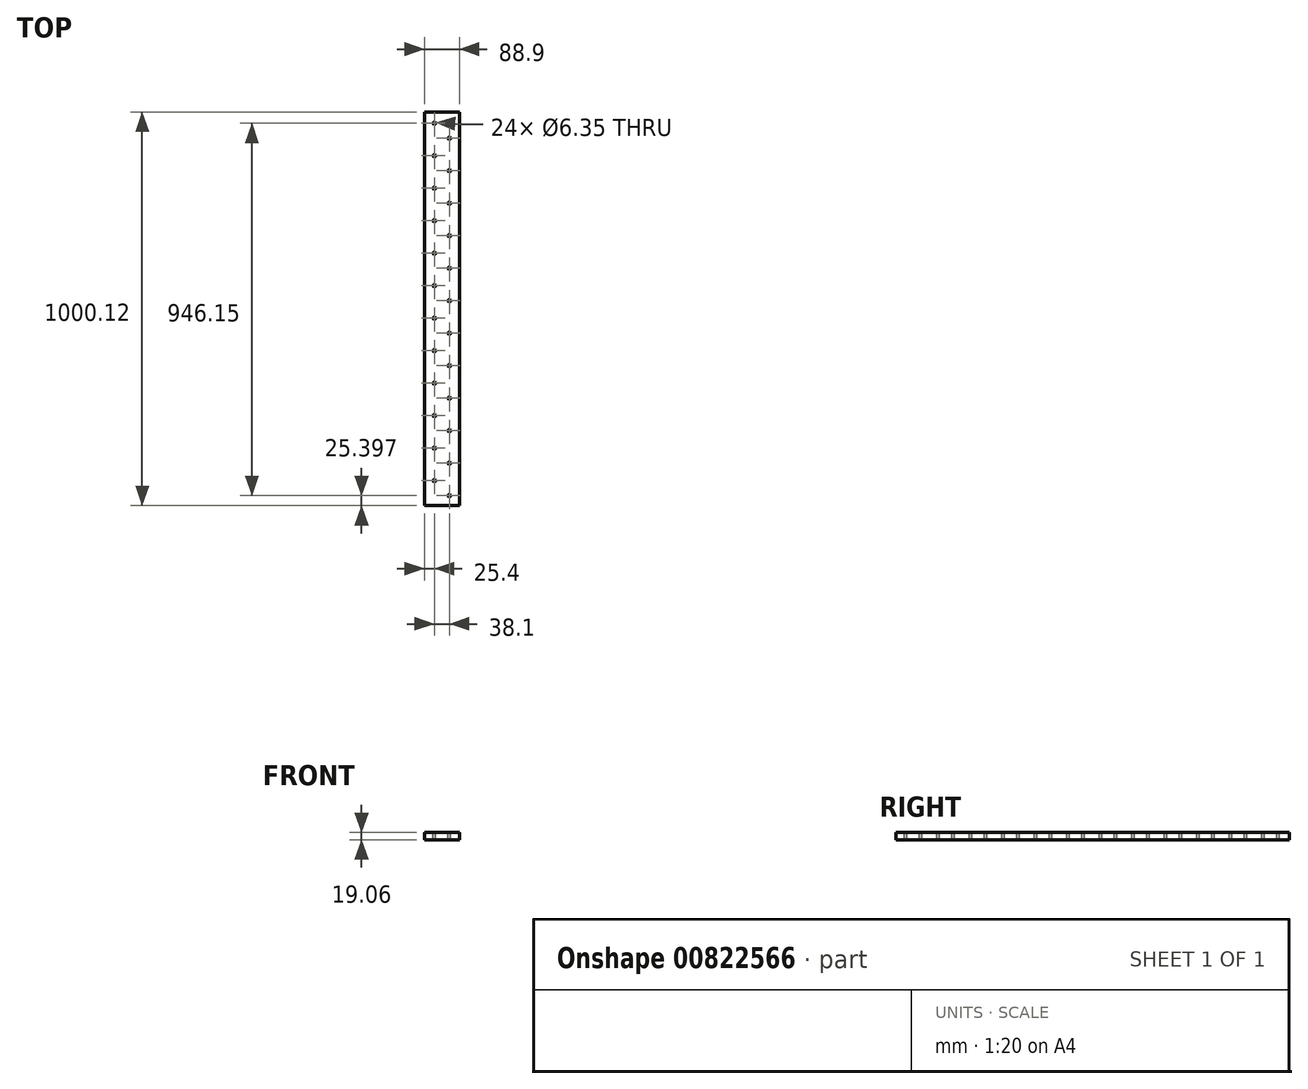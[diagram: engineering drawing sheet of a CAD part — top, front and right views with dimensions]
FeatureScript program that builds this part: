
annotation { "Feature Type Name" : "Feature", "Feature Type Description" : "" }
export const myFeature = defineFeature(function(context is Context, id is Id, definition is map)
    precondition{}
    {
        {
            var Q0;
            Q0=qCreatedBy(makeId("Front.planeOp"),FACE);
            var sketch = newSketch(context, id + "F0", { "sketchPlane" : qUnion([Q0])});
            skLineSegment(sketch, "E0.bottom", {"start": v(-44.45, 9.52) * mm, "end": v(44.45, 9.52) * mm});
            skLineSegment(sketch, "E0.top", {"start": v(-44.45, -9.53) * mm, "end": v(44.45, -9.53) * mm});
            skLineSegment(sketch, "E0.left", {"start": v(-44.45, 9.52) * mm, "end": v(-44.45, -9.53) * mm});
            skLineSegment(sketch, "E0.right", {"start": v(44.45, 9.52) * mm, "end": v(44.45, -9.53) * mm});
            skLineSegment(sketch, "E1", {"start": v(-44.45, -9.53) * mm, "end": v(44.45, 9.52) * mm, "construction": true});
            skSolve(sketch);
        }
        {
            var Q0;
            Q0=makeQuery(id+"F0.imprint","IMPRINT",FACE,{"disambiguationData":[TD([[makeQuery(id+"F0.imprint","IMPRINT",EDGE,{"derivedFrom":sQuery(id+"F0.wireOp",EDGE,"E0.bottom")}),-1.0]])]});
            extrude(context, id + "F1", {"entities" : qUnion([Q0]), "endBound" : BoundingType.SYMMETRIC, "depth" : 1000.12 * mm, "offsetDistance" : 25.4 * mm});
        }
        {
            var Q0;
            Q0=makeQuery(id+"F1.opExtrude","SWEPT_FACE",FACE,{"disambiguationData":[OSD([sQuery(id+"F0.wireOp",EDGE,"E0.bottom")])]});
            var sketch = newSketch(context, id + "F2", { "sketchPlane" : qUnion([Q0])});
            skLineSegment(sketch, "E2.bottom", {"start": v(-19.05, -436.56) * mm, "end": v(19.05, -436.56) * mm, "construction": true});
            skLineSegment(sketch, "E2.left", {"start": v(-19.05, -436.56) * mm, "end": v(-19.05, -474.66) * mm, "construction": true});
            skLineSegment(sketch, "E2.right", {"start": v(19.05, -436.56) * mm, "end": v(19.05, -474.66) * mm, "construction": true});
            skLineSegment(sketch, "E3", {"start": v(-19.05, -474.66) * mm, "end": v(19.05, -474.66) * mm, "construction": true});
            skLineSegment(sketch, "E4", {"start": v(0, -474.66) * mm, "end": v(0, -500.06) * mm, "construction": true});
            skCircle(sketch, "E5", {"center": v(19.05, -474.66) * mm, "radius": 3.18 * mm});
            skCircle(sketch, "E6", {"center": v(-19.05, -436.56) * mm, "radius": 3.18 * mm});
            skCircle(sketch, "E7.0.1.0", {"center": v(-19.05, -354.01) * mm, "radius": 3.18 * mm});
            skCircle(sketch, "E7.0.1.1", {"center": v(19.05, -392.11) * mm, "radius": 3.18 * mm});
            skCircle(sketch, "E7.0.2.0", {"center": v(-19.05, -271.46) * mm, "radius": 3.18 * mm});
            skCircle(sketch, "E7.0.2.1", {"center": v(19.05, -309.56) * mm, "radius": 3.18 * mm});
            skCircle(sketch, "E7.0.3.0", {"center": v(-19.05, -188.91) * mm, "radius": 3.18 * mm});
            skCircle(sketch, "E7.0.3.1", {"center": v(19.05, -227.01) * mm, "radius": 3.18 * mm});
            skCircle(sketch, "E7.0.4.0", {"center": v(-19.05, -106.36) * mm, "radius": 3.18 * mm});
            skCircle(sketch, "E7.0.4.1", {"center": v(19.05, -144.46) * mm, "radius": 3.18 * mm});
            skCircle(sketch, "E7.0.5.0", {"center": v(-19.05, -23.81) * mm, "radius": 3.18 * mm});
            skCircle(sketch, "E7.0.5.1", {"center": v(19.05, -61.91) * mm, "radius": 3.18 * mm});
            skCircle(sketch, "E7.0.6.0", {"center": v(-19.05, 58.74) * mm, "radius": 3.18 * mm});
            skCircle(sketch, "E7.0.6.1", {"center": v(19.05, 20.64) * mm, "radius": 3.18 * mm});
            skCircle(sketch, "E7.0.7.0", {"center": v(-19.05, 141.29) * mm, "radius": 3.18 * mm});
            skCircle(sketch, "E7.0.7.1", {"center": v(19.05, 103.19) * mm, "radius": 3.18 * mm});
            skCircle(sketch, "E7.0.8.0", {"center": v(-19.05, 223.84) * mm, "radius": 3.18 * mm});
            skCircle(sketch, "E7.0.8.1", {"center": v(19.05, 185.74) * mm, "radius": 3.18 * mm});
            skCircle(sketch, "E7.0.9.0", {"center": v(-19.05, 306.39) * mm, "radius": 3.18 * mm});
            skCircle(sketch, "E7.0.9.1", {"center": v(19.05, 268.29) * mm, "radius": 3.18 * mm});
            skCircle(sketch, "E7.0.10.0", {"center": v(-19.05, 388.94) * mm, "radius": 3.18 * mm});
            skCircle(sketch, "E7.0.10.1", {"center": v(19.05, 350.84) * mm, "radius": 3.18 * mm});
            skLineSegment(sketch, "E7.direction1", {"start": v(-19.05, -436.56) * mm, "end": v(8.37, -436.56) * mm, "construction": true});
            skLineSegment(sketch, "E7.direction2", {"start": v(-19.05, -436.56) * mm, "end": v(-19.05, -354.01) * mm, "construction": true});
            skCircle(sketch, "E8.0.0.11", {"center": v(-19.05, 471.49) * mm, "radius": 3.18 * mm});
            skCircle(sketch, "E8.2.0.11", {"center": v(19.05, 433.39) * mm, "radius": 3.18 * mm});
            skSolve(sketch);
        }
        {
            var Q0;
            Q0=qSketchRegion(id+"F2",true);
            extrude(context, id + "F3", {"entities" : qUnion([Q0]), "operationType" : NewBodyOperationType.REMOVE, "endBound" : BoundingType.UP_TO_NEXT, "oppositeDirection" : true, "depth" : 25.4 * mm, "offsetDistance" : 25.4 * mm});
        }
    });
